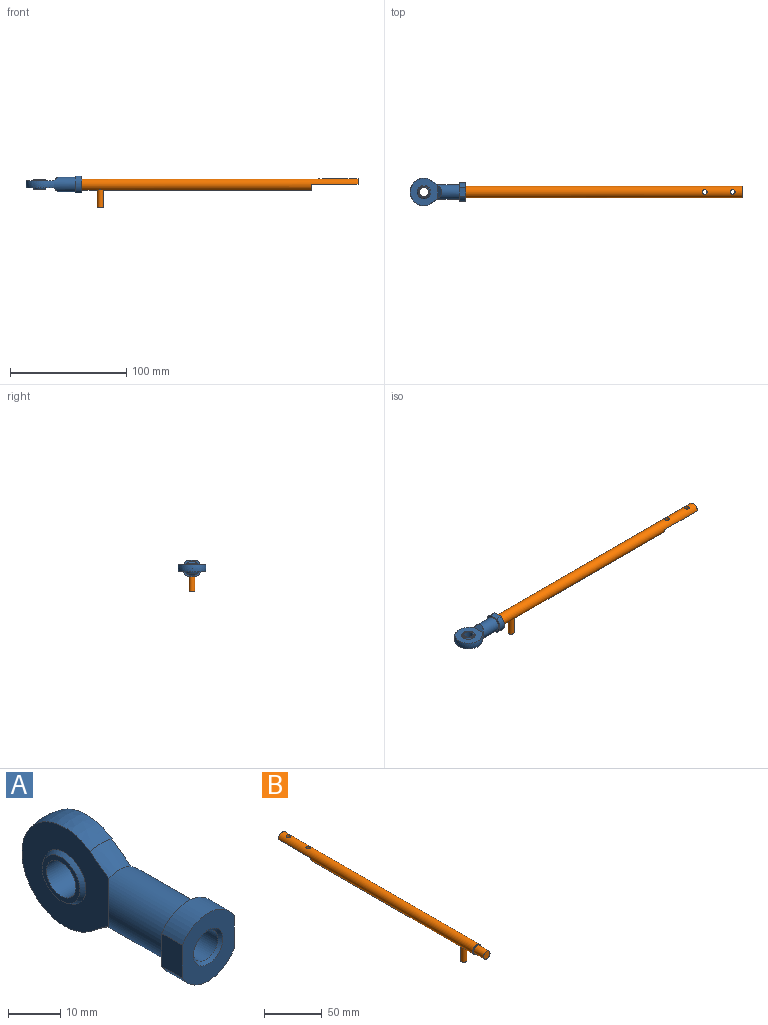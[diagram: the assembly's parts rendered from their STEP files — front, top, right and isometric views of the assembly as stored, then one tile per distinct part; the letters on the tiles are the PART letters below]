
ASSEMBLY  parts=2 mates=1
PART A: 23 faces, bbox 24.4x48.4x24.4 mm
  f0: sphere r=6.5mm, area 40.8mm2, adj f15,f16
  f1: sphere r=6.5mm, area 40.8mm2, adj f11,f17
  f2: cylinder r=6.25mm len=18.4mm, axis (0,1,0), area 665.8mm2, adj f3,f6,f9,f10,f14
  f3: cone r=6.25mm half-angle=35deg, axis (0,1,0), area 40mm2, adj f2,f4,f11,f15
  f4: sphere r=12mm, area 315.2mm2, adj f3,f6,f11,f15
  f5: cylinder r=8mm len=14mm, axis (0,1,0), area 95.5mm2, adj f7,f9,f12,f13
  f6: cone r=6.25mm half-angle=35deg, axis (0,1,0), area 40mm2, adj f2,f4,f11,f15
  f7: plane 16x14mm, normal (0,-1,0), area 140.3mm2, adj f5,f8,f12,f13,f19
  f8: cylinder r=8mm len=14mm, axis (0,1,0), area 95.5mm2, adj f7,f9,f12,f13
  f9: plane 16x14mm, normal (0,1,0), area 67.9mm2, adj f2,f5,f8,f12,f13
  f10: plane 10.97x3.25mm, normal (0.71,0.71,0), area 35.9mm2, adj f2,f11
  f11: plane 23.98x23.6mm, normal (1,0,0), area 333.8mm2, adj f1,f3,f4,f6,f10
  f12: plane 7.75x5.6mm, normal (-1,0,0), area 43.4mm2, adj f5,f7,f8,f9
  f13: plane 7.75x5.6mm, normal (1,0,0), area 43.4mm2, adj f5,f7,f8,f9
  f14: plane 10.97x3.25mm, normal (-0.71,0.71,0), area 35.9mm2, adj f2,f15
  f15: plane 23.98x23.6mm, normal (-1,0,0), area 333.8mm2, adj f0,f3,f4,f6,f14
  f16: plane 10.25x10.25mm, normal (-1,0,0), area 32.2mm2, adj f0,f18
  f17: plane 10.25x10.25mm, normal (1,0,0), area 32.2mm2, adj f1,f18
  f18: cylinder r=4mm len=8mm, axis (-1,0,0), area 201.1mm2, adj f16,f17
  f19: cone r=4mm half-angle=45deg, axis (0,-1,0), area 22mm2, adj f7,f20
  f20: cylinder r=3.32mm len=18.65mm, axis (0,1,0), area 389.4mm2, adj f19,f21
  f21: cone r=3.32mm half-angle=45deg, axis (0,1,0), area 22mm2, adj f20,f22
  f22: plane 8x8mm, normal (0,-1,0), area 50.3mm2, adj f21
PART B: 11 faces, bbox 10x250x25 mm
  f0: cylinder r=5mm len=238mm, axis (0,-1,0), area 6802.7mm2, adj f1,f2,f3,f4,f5,f6,f9
  f1: plane 10x5mm, normal (0,1,0), area 39.3mm2, adj f0,f2
  f2: plane 40x10mm, normal (0,0,-1), area 374.9mm2, adj f0,f1,f3,f4,f5
  f3: plane 10x5mm, normal (0,1,0), area 39.3mm2, adj f0,f2
  f4: cylinder r=2mm len=5mm, axis (0,0,-1), area 60.2mm2, adj f0,f2
  f5: cylinder r=2mm len=5mm, axis (0,0,-1), area 60.2mm2, adj f0,f2
  f6: cylinder r=2.5mm len=15.67mm, axis (0,0,1), area 240.8mm2, adj f0,f7
  f7: plane 5x5mm, normal (0,0,-1), area 19.6mm2, adj f6
  f8: cylinder r=4mm len=12mm, axis (0,-1,0), area 301.6mm2, adj f9,f10
  f9: plane 10x10mm, normal (0,-1,0), area 28.3mm2, adj f0,f8
  f10: plane 8x8mm, normal (0,-1,0), area 50.3mm2, adj f8
PLACE A rot(axis=(0.58,-0.58,0.58),120deg) t=(0.9,0,0.13)mm
PLACE B rot(axis=(0,0,-1),90deg) t=(24.9,0,-13.9)mm
MATE fastened A.f19 <-> B.f0  axis (1,0,0) through (36.9,0,0.13)mm
